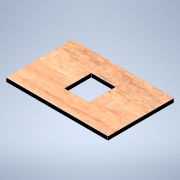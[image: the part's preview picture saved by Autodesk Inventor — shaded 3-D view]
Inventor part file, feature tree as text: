
AUTODESK INVENTOR PART (.ipt)
format: ipt  version: 2021 (Build 250183000, 183)  size: 121,344 bytes
history: native  units: mm
features: extrude x1, sketch x1
ambient origin geometry x8: Origin, YZ Plane, XZ Plane, XY Plane, X Axis, Y Axis, Z Axis, Center Point
bodies: Volumenkörper1 (feature_tree)
feature tree (2):
  extrude  "Extrusion1"  Depth=51.5mm
  sketch  "Skizze1"  dims[d0=79.5mm d1=51.5mm d2=3.0mm d3=0.0mm d4=19.0mm d5=21.0mm]
